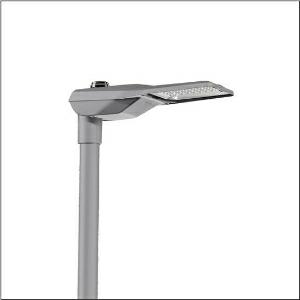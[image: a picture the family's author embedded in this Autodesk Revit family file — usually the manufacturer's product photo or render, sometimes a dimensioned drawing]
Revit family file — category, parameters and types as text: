
# Revit family: streetlight_sl_21_mini___stw1_0a_5xe6e47n08hb_d0ec
name_source: partatom
category: Lighting Fixtures
units: mm (PartAtom-declared; Revit-internal decimal feet)

## family parameters
Cut with Voids When Loaded = No
Host = Face
Light Source = No
Part Type = Normal
Room Calculation Point = No
Round Connector Dimension = Use Diameter
Shared = No

## types (1)
- --- (1 x LED, 9430 lm, 66 W, 4000K)
    Apparent Load = 66 VA
    CIE Flux Codes = 38 75 98 100 100
    Color Rendering = 70
    Color Temperature = 4000K
    Default Elevation = 1800 mm
    Description = Streetlight SL 21 mini, mast luminaire, primary light control with lens, of PMMA, primary optical cover: cover, of toughened safety glass, transparent, light distribution: STW1.0a, light emission: direct distribution, primary light characteristic: asymmetric, installation type: side-entry, LED, 3G 1.5mm², High Power LED, rated luminous flux: 9.430lm, luminous efficacy: 143lm/W, light colour: 740, colour temperature: 4000K, control gear: NEMA (7pin), control: overheat protection, pre-setting: linear dimming characteristic, constant luminous flux control, time-dependent luminous flux control, flexible luminous flux parameterisation, mains connection: 230..240V, AC, 50/60Hz, connection cable pre-assembled, cable length: 8,5m, wiring characteristics: H07RN-F, start of lifetime: 66W, end of service life: 69W, reduction: 30W, luminaire housing, of diecast aluminium (EN AC-44300), powder-coated, SITECO metallic grey (DB 702S), corrosivity category C5 high according to DIN EN ISO 12944, multi-level sealing system, sealing non-destructively replaceable, inclination adjustable: 0°, 5°, 10°, 15°, length: 628mm, width: 235mm, height: 110mm, spigot size: 42mm (side-entry), mounting height: 4..8m, protection rating (complete): IP66, insulation class (complete): insulation class I (protective earthing), certification: CE, ENEC, ENEC+, VDE, impact resistance: IK10, permissible operating ambient temperature for outdoor applications: -40..+50°C, standard-compliant lighting for roads and squares, packaging unit: 1 piece

Light Distribution: STW1.0a
    Height = 110 mm
    Lamp = 1 x LED
    Lamp Light Flux = 9430 lm
    Lamp Power = 66 W
    Lamp count = 1
    Length = 625 mm
    Luminous efficacy = 143 lm/W
    Manufacturer = Siteco
    ModVariant = No
    Model = 5XE6E47N08HB
    Number of Poles = 1
    OnlyDefault = Yes
    Power Factor = 1
    Product Name = Streetlight SL 21 mini | STW1.0a
    Product group = mast luminaire | pylon top
    ProductGroupID = 6100
    Protection Class = Protection class I
    Protection Degree = IP 66
    RLX_Detail_Level = 1
    RLX_Emergency_Light_Flux = 0 lm
    RLX_Emergency_Type = 0
    RLX_Emergency_Type_DB = No
    RlxData = <blob elided: 26233 chars, md5=a2ce5dd6>
    Socket = socket
    Standby Power = 0 W
    System Light Flux = 9430 lm
    System Power = 66 W
    Type Comments = factory setting: luminous flux: 100 % | dim-lin: 254 | 670 mA
    Type Image = l_1294379.jpg
    URL = http://relux.com
    VarID = @adj_135093
    Voltage = 0 V
    Weight = 0.00 kg
    Width = 234 mm

## geometry (parser evidence)
native form markers: Blend x4, Sweep x10
no freeform markers — native parametric forms only
